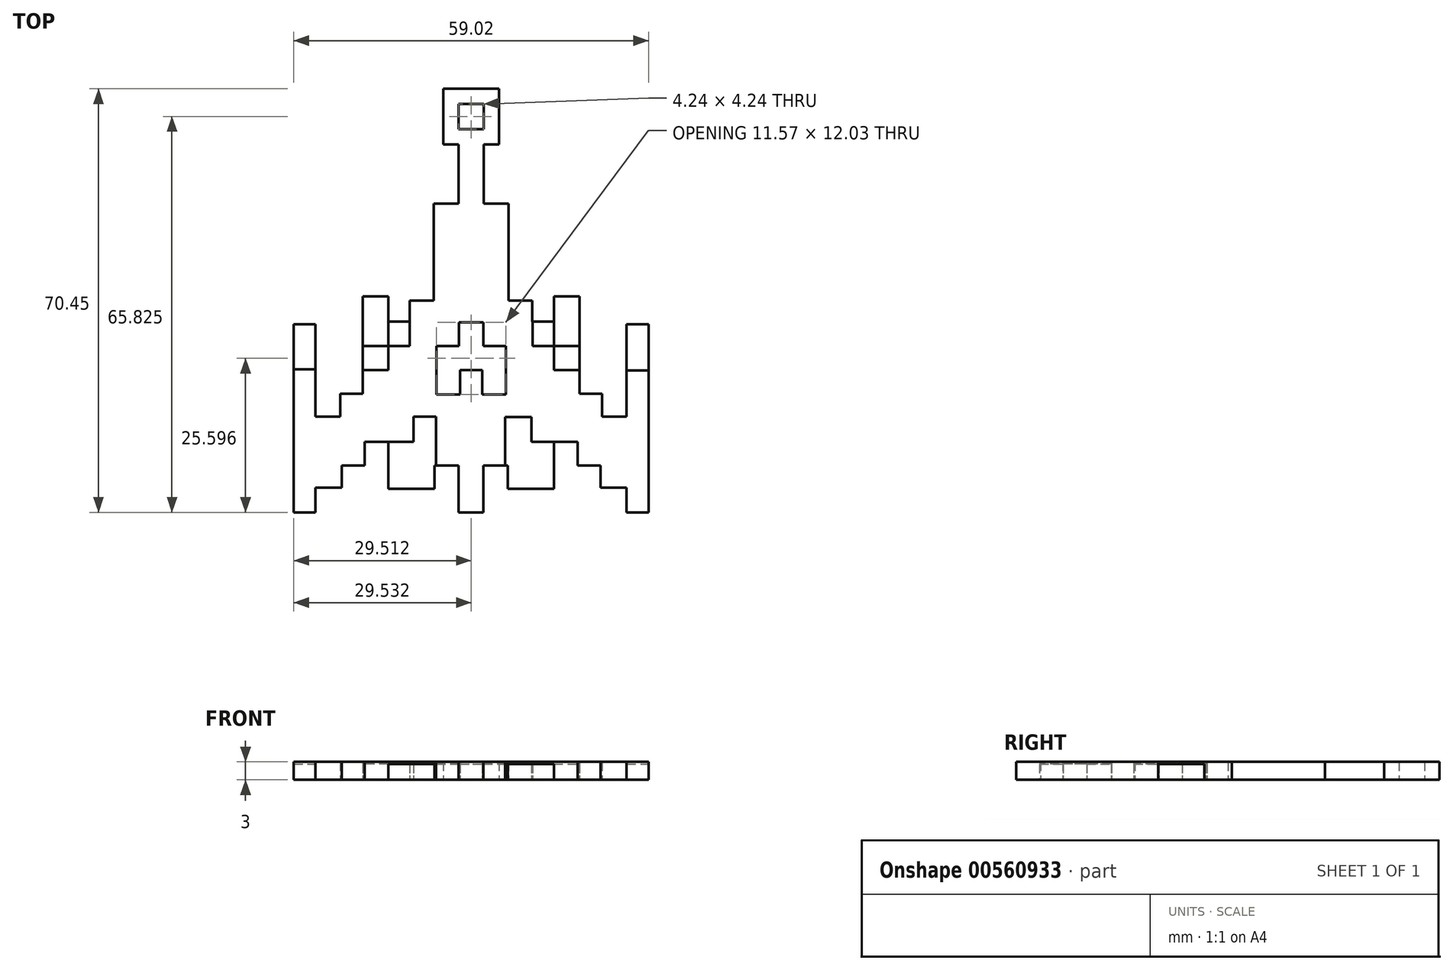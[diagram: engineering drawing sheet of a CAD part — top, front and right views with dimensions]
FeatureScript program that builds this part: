
annotation { "Feature Type Name" : "Feature", "Feature Type Description" : "" }
export const myFeature = defineFeature(function(context is Context, id is Id, definition is map)
    precondition{}
    {
        {
            var Q0;
            Q0=qCreatedBy(makeId("Top.planeOp"),FACE);
            var sketch = newSketch(context, id + "F0", { "sketchPlane" : qUnion([Q0])});
            skLineSegment(sketch, "E0", {"start": v(30.2, 67.42) * mm, "end": v(32.31, 67.42) * mm});
            skLineSegment(sketch, "E1", {"start": v(32.31, 67.42) * mm, "end": v(32.31, 55.06) * mm});
            skLineSegment(sketch, "E2", {"start": v(32.31, 55.06) * mm, "end": v(36.44, 55.06) * mm});
            skLineSegment(sketch, "E3", {"start": v(36.44, 55.06) * mm, "end": v(36.44, 38.96) * mm});
            skLineSegment(sketch, "E4", {"start": v(36.44, 38.96) * mm, "end": v(40.39, 38.96) * mm});
            skLineSegment(sketch, "E5", {"start": v(40.39, 38.96) * mm, "end": v(40.39, 35.46) * mm});
            skLineSegment(sketch, "E6", {"start": v(40.39, 35.46) * mm, "end": v(43.97, 35.46) * mm});
            skLineSegment(sketch, "E7", {"start": v(43.97, 35.46) * mm, "end": v(43.97, 47.05) * mm});
            skLineSegment(sketch, "E8", {"start": v(43.97, 47.05) * mm, "end": v(48.21, 47.05) * mm});
            skLineSegment(sketch, "E9", {"start": v(48.21, 47.05) * mm, "end": v(48.21, 23.44) * mm});
            skLineSegment(sketch, "E10", {"start": v(48.21, 23.44) * mm, "end": v(51.96, 23.44) * mm});
            skLineSegment(sketch, "E11", {"start": v(51.96, 23.44) * mm, "end": v(51.96, 19.6) * mm});
            skLineSegment(sketch, "E12", {"start": v(51.96, 19.6) * mm, "end": v(56.07, 19.6) * mm});
            skLineSegment(sketch, "E13", {"start": v(56.07, 19.6) * mm, "end": v(56.07, 35.02) * mm});
            skLineSegment(sketch, "E14", {"start": v(56.07, 35.02) * mm, "end": v(59.7, 35.02) * mm});
            skLineSegment(sketch, "E15", {"start": v(59.7, 35.02) * mm, "end": v(59.7, 3.71) * mm});
            skLineSegment(sketch, "E16", {"start": v(59.7, 3.71) * mm, "end": v(56.07, 3.71) * mm});
            skLineSegment(sketch, "E17", {"start": v(56.07, 3.71) * mm, "end": v(56.07, 7.81) * mm});
            skLineSegment(sketch, "E18", {"start": v(56.07, 7.81) * mm, "end": v(51.7, 7.81) * mm});
            skLineSegment(sketch, "E19", {"start": v(51.7, 7.81) * mm, "end": v(51.7, 11.49) * mm});
            skLineSegment(sketch, "E20", {"start": v(51.7, 11.49) * mm, "end": v(47.92, 11.49) * mm});
            skLineSegment(sketch, "E21", {"start": v(47.92, 11.49) * mm, "end": v(47.92, 15.45) * mm});
            skLineSegment(sketch, "E22", {"start": v(47.92, 15.45) * mm, "end": v(43.98, 15.45) * mm});
            skLineSegment(sketch, "E23", {"start": v(43.98, 15.45) * mm, "end": v(43.98, 7.6) * mm});
            skLineSegment(sketch, "E24", {"start": v(43.98, 7.6) * mm, "end": v(36.3, 7.6) * mm});
            skLineSegment(sketch, "E25", {"start": v(36.3, 7.6) * mm, "end": v(36.3, 11.5) * mm});
            skLineSegment(sketch, "E26", {"start": v(36.3, 11.5) * mm, "end": v(32.25, 11.5) * mm});
            skLineSegment(sketch, "E27", {"start": v(32.25, 11.5) * mm, "end": v(32.25, 3.71) * mm});
            skLineSegment(sketch, "E28", {"start": v(32.25, 3.71) * mm, "end": v(30.43, 3.71) * mm});
            skLineSegment(sketch, "E29", {"start": v(32.31, 67.42) * mm, "end": v(30.2, 67.42) * mm});
            skLineSegment(sketch, "E30", {"start": v(30.2, 67.42) * mm, "end": v(30.2, 58.68) * mm, "construction": true});
            skPoint(sketch, "E31.orphan", {"position": v(28.07, 67.42) * mm});
            skPoint(sketch, "E32.orphan", {"position": v(28.61, 3.71) * mm});
            skLineSegment(sketch, "E33.MirrorCS", {"start": v(30.2, 67.42) * mm, "end": v(28.07, 67.42) * mm});
            skLineSegment(sketch, "E34.MirrorCS", {"start": v(28.07, 67.42) * mm, "end": v(28.07, 55.06) * mm});
            skLineSegment(sketch, "E35.MirrorCS", {"start": v(28.07, 55.06) * mm, "end": v(23.95, 55.06) * mm});
            skLineSegment(sketch, "E36.MirrorCS", {"start": v(23.95, 55.06) * mm, "end": v(23.95, 38.96) * mm});
            skLineSegment(sketch, "E37.MirrorCS", {"start": v(23.95, 38.96) * mm, "end": v(20, 38.96) * mm});
            skLineSegment(sketch, "E38.MirrorCS", {"start": v(20, 35.46) * mm, "end": v(16.42, 35.46) * mm});
            skLineSegment(sketch, "E39.MirrorCS", {"start": v(16.42, 35.46) * mm, "end": v(16.42, 47.05) * mm});
            skLineSegment(sketch, "E40.MirrorCS", {"start": v(16.42, 47.05) * mm, "end": v(12.17, 47.05) * mm});
            skLineSegment(sketch, "E41.MirrorCS", {"start": v(12.17, 47.05) * mm, "end": v(12.17, 23.44) * mm});
            skLineSegment(sketch, "E42.MirrorCS", {"start": v(12.17, 23.44) * mm, "end": v(8.42, 23.44) * mm});
            skLineSegment(sketch, "E43.MirrorCS", {"start": v(8.42, 23.44) * mm, "end": v(8.42, 19.6) * mm});
            skLineSegment(sketch, "E44.MirrorCS", {"start": v(8.42, 19.6) * mm, "end": v(4.32, 19.6) * mm});
            skLineSegment(sketch, "E45.MirrorCS", {"start": v(4.32, 19.6) * mm, "end": v(4.32, 35.02) * mm});
            skLineSegment(sketch, "E46.MirrorCS", {"start": v(4.32, 35.02) * mm, "end": v(0.68, 35.02) * mm});
            skLineSegment(sketch, "E47.MirrorCS", {"start": v(0.68, 35.02) * mm, "end": v(0.68, 3.71) * mm});
            skLineSegment(sketch, "E48.MirrorCS", {"start": v(0.68, 3.71) * mm, "end": v(4.32, 3.71) * mm});
            skLineSegment(sketch, "E49.MirrorCS", {"start": v(4.32, 3.71) * mm, "end": v(4.32, 7.81) * mm});
            skLineSegment(sketch, "E50.MirrorCS", {"start": v(4.32, 7.81) * mm, "end": v(8.7, 7.81) * mm});
            skLineSegment(sketch, "E51.MirrorCS", {"start": v(8.7, 7.81) * mm, "end": v(8.7, 11.49) * mm});
            skLineSegment(sketch, "E52.MirrorCS", {"start": v(8.7, 11.49) * mm, "end": v(12.47, 11.49) * mm});
            skLineSegment(sketch, "E53.MirrorCS", {"start": v(12.47, 11.49) * mm, "end": v(12.47, 15.45) * mm});
            skLineSegment(sketch, "E54.MirrorCS", {"start": v(12.47, 15.45) * mm, "end": v(16.4, 15.45) * mm});
            skLineSegment(sketch, "E55.MirrorCS", {"start": v(16.4, 15.45) * mm, "end": v(16.4, 7.6) * mm});
            skLineSegment(sketch, "E56.MirrorCS", {"start": v(16.4, 7.6) * mm, "end": v(24.08, 7.6) * mm});
            skLineSegment(sketch, "E57.MirrorCS", {"start": v(24.08, 7.6) * mm, "end": v(24.08, 11.5) * mm});
            skLineSegment(sketch, "E58.MirrorCS", {"start": v(24.08, 11.5) * mm, "end": v(28.13, 11.5) * mm});
            skLineSegment(sketch, "E59.MirrorCS", {"start": v(28.13, 11.5) * mm, "end": v(28.13, 3.71) * mm});
            skLineSegment(sketch, "E60.MirrorCS", {"start": v(28.13, 3.71) * mm, "end": v(29.95, 3.71) * mm});
            skLineSegment(sketch, "E61.MirrorCS", {"start": v(20, 38.96) * mm, "end": v(20, 35.46) * mm});
            skLineSegment(sketch, "E62", {"start": v(29.95, 3.71) * mm, "end": v(30.43, 3.71) * mm});
            skLineSegment(sketch, "E63", {"start": v(16.42, 35.46) * mm, "end": v(16.42, 31.37) * mm});
            skLineSegment(sketch, "E64", {"start": v(16.42, 31.37) * mm, "end": v(20, 31.37) * mm});
            skLineSegment(sketch, "E65", {"start": v(20, 35.46) * mm, "end": v(20, 31.37) * mm});
            skPoint(sketch, "E66.orphan", {"position": v(20.16, 31.37) * mm});
            skLineSegment(sketch, "E67", {"start": v(16.42, 31.37) * mm, "end": v(16.42, 27.35) * mm});
            skLineSegment(sketch, "E68", {"start": v(16.42, 27.35) * mm, "end": v(12.17, 27.35) * mm});
            skLineSegment(sketch, "E69", {"start": v(16.42, 31.37) * mm, "end": v(12.17, 31.37) * mm});
            skLineSegment(sketch, "E70", {"start": v(28.17, 35.32) * mm, "end": v(28.17, 31.36) * mm});
            skLineSegment(sketch, "E71", {"start": v(28.17, 31.36) * mm, "end": v(24.43, 31.36) * mm});
            skLineSegment(sketch, "E72", {"start": v(24.43, 31.36) * mm, "end": v(24.43, 23.3) * mm});
            skLineSegment(sketch, "E73", {"start": v(24.43, 23.3) * mm, "end": v(28.36, 23.3) * mm});
            skLineSegment(sketch, "E74", {"start": v(28.36, 23.3) * mm, "end": v(28.36, 27.35) * mm});
            skLineSegment(sketch, "E75", {"start": v(28.36, 27.35) * mm, "end": v(32.06, 27.35) * mm});
            skLineSegment(sketch, "E76", {"start": v(30.21, 27.35) * mm, "end": v(30.21, 29.19) * mm, "construction": true});
            skLineSegment(sketch, "E77.MirrorCS", {"start": v(36, 23.3) * mm, "end": v(32.06, 23.3) * mm});
            skLineSegment(sketch, "E78.MirrorCS", {"start": v(36, 31.36) * mm, "end": v(36, 23.3) * mm});
            skLineSegment(sketch, "E79.MirrorCS", {"start": v(32.06, 23.3) * mm, "end": v(32.06, 27.35) * mm});
            skLineSegment(sketch, "E80.MirrorCS", {"start": v(32.25, 31.36) * mm, "end": v(36, 31.36) * mm});
            skLineSegment(sketch, "E81.MirrorCS", {"start": v(32.25, 35.32) * mm, "end": v(32.25, 31.36) * mm});
            skLineSegment(sketch, "E82.MirrorCS", {"start": v(44, 31.37) * mm, "end": v(40.43, 31.37) * mm});
            skLineSegment(sketch, "E83.MirrorCS", {"start": v(40.43, 35.46) * mm, "end": v(40.43, 31.37) * mm});
            skLineSegment(sketch, "E84.MirrorCS", {"start": v(44, 27.35) * mm, "end": v(48.25, 27.35) * mm});
            skLineSegment(sketch, "E85.MirrorCS", {"start": v(44, 31.37) * mm, "end": v(48.25, 31.37) * mm});
            skLineSegment(sketch, "E86", {"start": v(28.17, 35.32) * mm, "end": v(32.25, 35.32) * mm});
            skLineSegment(sketch, "E87", {"start": v(12.17, 39.6) * mm, "end": v(16.42, 39.6) * mm});
            skLineSegment(sketch, "E88", {"start": v(0.68, 27.5) * mm, "end": v(4.32, 27.5) * mm});
            skLineSegment(sketch, "E89", {"start": v(56.07, 27.31) * mm, "end": v(59.7, 27.31) * mm});
            skLineSegment(sketch, "E90.MirrorCS", {"start": v(48.25, 39.6) * mm, "end": v(44, 39.6) * mm});
            skLineSegment(sketch, "E91", {"start": v(16.4, 15.45) * mm, "end": v(20.59, 15.45) * mm});
            skLineSegment(sketch, "E92", {"start": v(20.59, 15.45) * mm, "end": v(20.59, 19.62) * mm});
            skLineSegment(sketch, "E93", {"start": v(20.59, 19.62) * mm, "end": v(24.33, 19.62) * mm});
            skLineSegment(sketch, "E94", {"start": v(24.33, 19.62) * mm, "end": v(24.33, 11.5) * mm});
            skLineSegment(sketch, "E95", {"start": v(43.98, 15.45) * mm, "end": v(40.24, 15.45) * mm});
            skLineSegment(sketch, "E96", {"start": v(40.24, 15.45) * mm, "end": v(40.24, 19.53) * mm});
            skLineSegment(sketch, "E97", {"start": v(40.24, 19.53) * mm, "end": v(35.84, 19.53) * mm});
            skLineSegment(sketch, "E98", {"start": v(35.84, 19.53) * mm, "end": v(35.84, 11.5) * mm});
            skLineSegment(sketch, "E99", {"start": v(44, 39.6) * mm, "end": v(43.97, 39.6) * mm});
            skLineSegment(sketch, "E100", {"start": v(43.97, 35.46) * mm, "end": v(43.97, 31.37) * mm});
            skLineSegment(sketch, "E101", {"start": v(28.07, 67.42) * mm, "end": v(28.07, 71.66) * mm});
            skLineSegment(sketch, "E102.MirrorCS", {"start": v(32.31, 67.42) * mm, "end": v(32.31, 71.66) * mm});
            skLineSegment(sketch, "E103", {"start": v(28.07, 71.66) * mm, "end": v(32.31, 71.66) * mm});
            skLineSegment(sketch, "E104", {"start": v(28.07, 64.92) * mm, "end": v(25.57, 64.92) * mm});
            skLineSegment(sketch, "E105", {"start": v(25.57, 64.92) * mm, "end": v(25.57, 74.16) * mm});
            skLineSegment(sketch, "E106", {"start": v(25.57, 74.16) * mm, "end": v(34.81, 74.16) * mm});
            skLineSegment(sketch, "E107", {"start": v(34.81, 74.16) * mm, "end": v(34.81, 64.92) * mm});
            skLineSegment(sketch, "E108", {"start": v(34.81, 64.92) * mm, "end": v(32.31, 64.92) * mm});
            skLineSegment(sketch, "E109", {"start": v(43.97, 31.37) * mm, "end": v(43.97, 27.35) * mm});
            skLineSegment(sketch, "E110", {"start": v(43.97, 27.35) * mm, "end": v(44, 27.35) * mm});
            skSolve(sketch);
        }
        {
            var Q0;
            Q0=makeQuery(id+"F0.imprint","IMPRINT",FACE,{"disambiguationData":[TD([[makeQuery(id+"F0.imprint","IMPRINT",EDGE,{"derivedFrom":sQuery(id+"F0.wireOp",EDGE,"E1")}),-1.0]])]});
            var Q1;
            {var subQ6=sQuery(id+"F0.wireOp",EDGE,"E99");Q1=makeQuery(id+"F0.imprint","IMPRINT",FACE,{"disambiguationData":[TD([[makeQuery(id+"F0.imprint","IMPRINT",EDGE,{"derivedFrom":subQ6}),1.0]])]});}
            var Q2;
            {var subQ1=sQuery(id+"F0.wireOp",EDGE,"E63");Q2=makeQuery(id+"F0.imprint","IMPRINT",FACE,{"disambiguationData":[TD([[makeQuery(id+"F0.imprint","IMPRINT",EDGE,{"derivedFrom":subQ1}),-1.0]])]});}
            var Q3;
            {var subQ0=sQuery(id+"F0.wireOp",EDGE,"E101");Q3=makeQuery(id+"F0.imprint","IMPRINT",FACE,{"disambiguationData":[TD([[makeQuery(id+"F0.imprint","IMPRINT",EDGE,{"derivedFrom":subQ0}),1.0]])]});}
            extrude(context, id + "F1", {"entities" : qUnion([Q0, Q1, Q2, Q3]), "depth" : 3 * mm, "offsetDistance" : 25 * mm});
        }
        {
            var Q0;
            {var subQ0=sQuery(id+"F0.wireOp",EDGE,"E46.MirrorCS");Q0=makeQuery(id+"F0.imprint","IMPRINT",FACE,{"disambiguationData":[TD([[makeQuery(id+"F0.imprint","IMPRINT",EDGE,{"derivedFrom":subQ0}),1.0]])]});}
            var Q1;
            Q1=makeQuery(id+"F0.imprint","IMPRINT",FACE,{"disambiguationData":[TD([[makeQuery(id+"F0.imprint","IMPRINT",EDGE,{"derivedFrom":sQuery(id+"F0.wireOp",EDGE,"E70")}),1.0]])]});
            var Q2;
            {var subQ2=sQuery(id+"F0.wireOp",EDGE,"E83.MirrorCS");Q2=makeQuery(id+"F0.imprint","IMPRINT",FACE,{"disambiguationData":[TD([[makeQuery(id+"F0.imprint","IMPRINT",EDGE,{"derivedFrom":subQ2}),1.0]])]});}
            var Q3;
            {var subQ5=sQuery(id+"F0.wireOp",EDGE,"b0de0051-c1c2-443f-bbb5-749214450e5d0.MirrorCS");Q3=makeQuery(id+"F0.imprint","IMPRINT",FACE,{"disambiguationData":[TD([[makeQuery(id+"F0.imprint","IMPRINT",EDGE,{"derivedFrom":subQ5}),1.0]])]});}
            var Q4;
            {var subQ0=sQuery(id+"F0.wireOp",EDGE,"E14");Q4=makeQuery(id+"F0.imprint","IMPRINT",FACE,{"disambiguationData":[TD([[makeQuery(id+"F0.imprint","IMPRINT",EDGE,{"derivedFrom":subQ0}),-1.0]])]});}
            var Q5;
            Q5=makeQuery(id+"F0.imprint","IMPRINT",FACE,{"disambiguationData":[TD([[makeQuery(id+"F0.imprint","IMPRINT",EDGE,{"derivedFrom":sQuery(id+"F0.wireOp",EDGE,"E23")}),-1.0]])]});
            var Q6;
            Q6=makeQuery(id+"F0.imprint","IMPRINT",FACE,{"disambiguationData":[TD([[makeQuery(id+"F0.imprint","IMPRINT",EDGE,{"derivedFrom":sQuery(id+"F0.wireOp",EDGE,"E55.MirrorCS")}),1.0]])]});
            var Q7;
            Q7=makeQuery(id+"F0.imprint","IMPRINT",FACE,{"disambiguationData":[TD([[makeQuery(id+"F0.imprint","IMPRINT",EDGE,{"derivedFrom":sQuery(id+"F0.wireOp",EDGE,"E67")}),-1.0]])]});
            var Q8;
            Q8=makeQuery(id+"F0.imprint","IMPRINT",FACE,{"disambiguationData":[TD([[makeQuery(id+"F0.imprint","IMPRINT",EDGE,{"derivedFrom":sQuery(id+"F0.wireOp",EDGE,"E38.MirrorCS")}),1.0]])]});
            var Q9;
            {var subQ8=sQuery(id+"F0.wireOp",EDGE,"E109");Q9=makeQuery(id+"F0.imprint","IMPRINT",FACE,{"disambiguationData":[TD([[makeQuery(id+"F0.imprint","IMPRINT",EDGE,{"derivedFrom":subQ8}),1.0]])]});}
            extrude(context, id + "F2", {"entities" : qUnion([Q0, Q1, Q2, Q3, Q4, Q5, Q6, Q7, Q8, Q9]), "depth" : 2.6 * mm, "offsetDistance" : 25 * mm});
        }
    });
